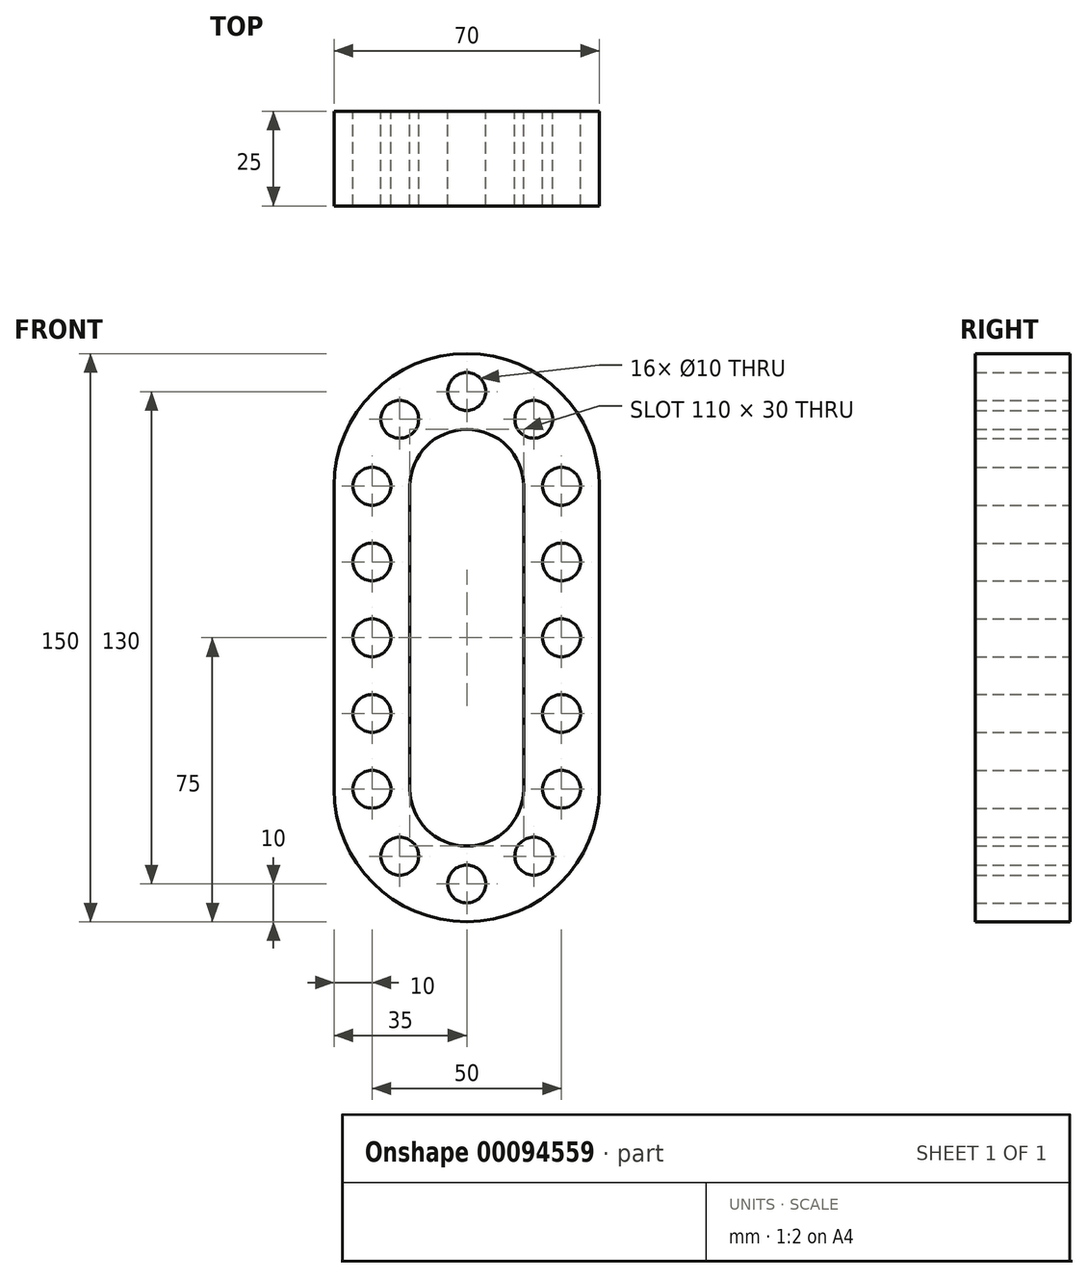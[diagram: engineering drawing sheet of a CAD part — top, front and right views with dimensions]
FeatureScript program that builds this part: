
annotation { "Feature Type Name" : "Feature", "Feature Type Description" : "" }
export const myFeature = defineFeature(function(context is Context, id is Id, definition is map)
    precondition{}
    {
        {
            var Q0;
            Q0=qCreatedBy(makeId("Front.planeOp"),FACE);
            var sketch = newSketch(context, id + "F0", { "sketchPlane" : qUnion([Q0])});
            skPoint(sketch, "E0", {"position": v(-25, 40) * mm});
            skLineSegment(sketch, "E1", {"start": v(-25, 40) * mm, "end": v(-25, 0) * mm, "construction": true});
            skArc(sketch, "E2", {"start": v(0, 65) * mm, "mid": v(-17.68, 57.68) * mm, "end": v(-25, 40) * mm, "construction": true});
            skArc(sketch, "E3.0.startCap", {"start": v(0, 75) * mm, "mid": v(10, 65) * mm, "end": v(0, 55) * mm, "construction": true});
            skArc(sketch, "E3.0.endCap", {"start": v(-15, 40) * mm, "mid": v(-25, 30) * mm, "end": v(-35, 40) * mm, "construction": true});
            skArc(sketch, "E3.0.left", {"start": v(0, 55) * mm, "mid": v(-10.6, 50.6) * mm, "end": v(-15, 40) * mm});
            skArc(sketch, "E3.0.right", {"start": v(0, 75) * mm, "mid": v(-24.75, 64.75) * mm, "end": v(-35, 40) * mm});
            skArc(sketch, "E3.1.startCap", {"start": v(-35, 40) * mm, "mid": v(-25, 50) * mm, "end": v(-15, 40) * mm, "construction": true});
            skArc(sketch, "E3.1.endCap", {"start": v(-15, 0) * mm, "mid": v(-25, -10) * mm, "end": v(-35, 0) * mm, "construction": true});
            skLineSegment(sketch, "E3.1.left", {"start": v(-15, 40) * mm, "end": v(-15, 0) * mm});
            skLineSegment(sketch, "E3.1.right", {"start": v(-35, 40) * mm, "end": v(-35, 0) * mm});
            skCircle(sketch, "E4", {"center": v(-25, 40) * mm, "radius": 5 * mm});
            skCircle(sketch, "E5.0.1.0", {"center": v(-25, 20) * mm, "radius": 5 * mm});
            skLineSegment(sketch, "E5.0.1.1", {"start": v(-25, 20) * mm, "end": v(-25, -20) * mm, "construction": true});
            skCircle(sketch, "E5.0.2.0", {"center": v(-25, 0) * mm, "radius": 5 * mm});
            skLineSegment(sketch, "E5.0.2.1", {"start": v(-25, 0) * mm, "end": v(-25, -40) * mm, "construction": true});
            skLineSegment(sketch, "E5.direction1", {"start": v(-25, 40) * mm, "end": v(0, 40) * mm, "construction": true});
            skLineSegment(sketch, "E5.direction2", {"start": v(-25, 40) * mm, "end": v(-25, 20) * mm, "construction": true});
            skCircle(sketch, "E6", {"center": v(0, 65) * mm, "radius": 5 * mm});
            skCircle(sketch, "E7", {"center": v(-17.68, 57.68) * mm, "radius": 5 * mm});
            skLineSegment(sketch, "E8", {"start": v(0, 75) * mm, "end": v(0, 70) * mm});
            skLineSegment(sketch, "E9", {"start": v(0, 55) * mm, "end": v(0, 60) * mm});
            skLineSegment(sketch, "E10", {"start": v(-15, 0) * mm, "end": v(-20, 0) * mm});
            skLineSegment(sketch, "E11", {"start": v(-35, 0) * mm, "end": v(-30, 0) * mm});
            skSolve(sketch);
        }
        {
            var Q0;
            Q0=makeQuery(id+"F0.imprint","IMPRINT",FACE,{"disambiguationData":[TD([[makeQuery(id+"F0.imprint","IMPRINT",EDGE,{"derivedFrom":sQuery(id+"F0.wireOp",EDGE,"E3.0.left")}),-1.0]])]});
            extrude(context, id + "F1", {"entities" : qUnion([Q0]), "depth" : 25 * mm});
        }
        {
            var Q0;
            Q0=makeQuery(id+"F1.opExtrude","SWEPT_BODY",BODY,{"disambiguationData":[OSD([sQuery(id+"F0.wireOp",EDGE,"E3.0.left"),sQuery(id+"F0.wireOp",EDGE,"E3.0.right"),sQuery(id+"F0.wireOp",EDGE,"E3.1.left"),sQuery(id+"F0.wireOp",EDGE,"E3.1.right"),sQuery(id+"F0.wireOp",EDGE,"E4"),sQuery(id+"F0.wireOp",EDGE,"E5.0.1.0"),sQuery(id+"F0.wireOp",EDGE,"E5.0.2.0"),sQuery(id+"F0.wireOp",EDGE,"E6"),sQuery(id+"F0.wireOp",EDGE,"E7"),sQuery(id+"F0.wireOp",EDGE,"E8"),sQuery(id+"F0.wireOp",EDGE,"E9"),sQuery(id+"F0.wireOp",EDGE,"E10"),sQuery(id+"F0.wireOp",EDGE,"E11")])]});
            var Q1;
            Q1=qCreatedBy(makeId("Right.planeOp"),FACE);
            mirror(context, id + "F2", {"operationType" : NewBodyOperationType.ADD, "entities" : qUnion([Q0]), "mirrorPlane" : qUnion([Q1])});
        }
        {
            var Q0;
            Q0=makeQuery(id+"F1.opExtrude","SWEPT_BODY",BODY,{"disambiguationData":[OSD([sQuery(id+"F0.wireOp",EDGE,"E3.0.left"),sQuery(id+"F0.wireOp",EDGE,"E3.0.right"),sQuery(id+"F0.wireOp",EDGE,"E3.1.left"),sQuery(id+"F0.wireOp",EDGE,"E3.1.right"),sQuery(id+"F0.wireOp",EDGE,"E4"),sQuery(id+"F0.wireOp",EDGE,"E5.0.1.0"),sQuery(id+"F0.wireOp",EDGE,"E5.0.2.0"),sQuery(id+"F0.wireOp",EDGE,"E6"),sQuery(id+"F0.wireOp",EDGE,"E7"),sQuery(id+"F0.wireOp",EDGE,"E8"),sQuery(id+"F0.wireOp",EDGE,"E9"),sQuery(id+"F0.wireOp",EDGE,"E10"),sQuery(id+"F0.wireOp",EDGE,"E11")])]});
            var Q1;
            Q1=qCreatedBy(makeId("Top.planeOp"),FACE);
            mirror(context, id + "F3", {"operationType" : NewBodyOperationType.ADD, "entities" : qUnion([Q0]), "mirrorPlane" : qUnion([Q1])});
        }
    });
